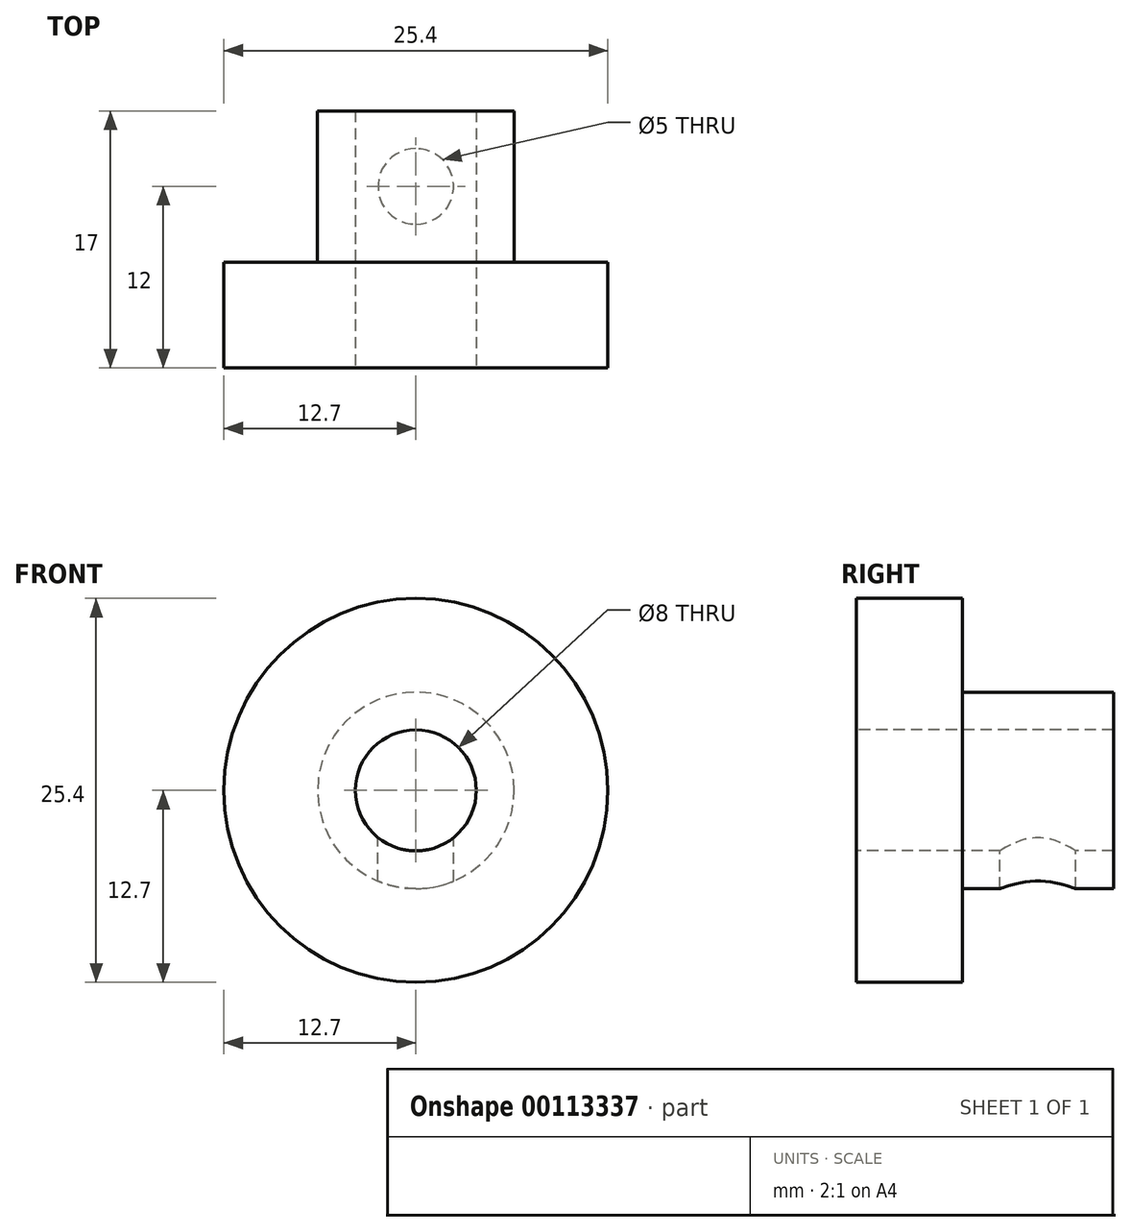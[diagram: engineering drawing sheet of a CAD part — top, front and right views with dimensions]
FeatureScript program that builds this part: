
annotation { "Feature Type Name" : "Feature", "Feature Type Description" : "" }
export const myFeature = defineFeature(function(context is Context, id is Id, definition is map)
    precondition{}
    {
        {
            var Q0;
            Q0=qCreatedBy(makeId("Front.planeOp"),FACE);
            var sketch = newSketch(context, id + "F0", { "sketchPlane" : qUnion([Q0])});
            skCircle(sketch, "E0", {"center": v(0, 0) * mm, "radius": 12.7 * mm});
            skSolve(sketch);
        }
        {
            var Q0;
            Q0=makeQuery(id+"F0.imprint","IMPRINT",FACE,{"disambiguationData":[TD([[makeQuery(id+"F0.imprint","IMPRINT",EDGE,{"derivedFrom":sQuery(id+"F0.wireOp",EDGE,"E0")}),1.0]])]});
            extrude(context, id + "F1", {"entities" : qUnion([Q0]), "depth" : 7 * mm});
        }
        {
            var Q0;
            Q0=qCreatedBy(makeId("Front.planeOp"),FACE);
            var sketch = newSketch(context, id + "F2", { "sketchPlane" : qUnion([Q0])});
            skCircle(sketch, "E1", {"center": v(0, 0) * mm, "radius": 6.5 * mm});
            skSolve(sketch);
        }
        {
            var Q0;
            Q0 = qSketchRegion(id + "F2", true);
            extrude(context, id + "F3", {"entities" : qUnion([Q0]), "operationType" : NewBodyOperationType.ADD, "oppositeDirection" : true, "depth" : 10 * mm});
        }
        {
            var Q0;
            Q0=qCreatedBy(makeId("Front.planeOp"),FACE);
            var sketch = newSketch(context, id + "F4", { "sketchPlane" : qUnion([Q0])});
            skCircle(sketch, "E2", {"center": v(0, 0) * mm, "radius": 4 * mm});
            skSolve(sketch);
        }
        {
            var Q0;
            Q0 = qSketchRegion(id + "F4", true);
            extrude(context, id + "F5", {"entities" : qUnion([Q0]), "operationType" : NewBodyOperationType.REMOVE, "endBound" : BoundingType.THROUGH_ALL, "oppositeDirection" : true, "depth" : 25 * mm});
        }
        {
            var Q0;
            Q0=makeQuery(id+"F5.boolean.opBoolean","COPY",FACE,{"derivedFrom":makeQuery(id+"F5.opExtrude","CAP_FACE",FACE,{"disambiguationData":[OSD([sQuery(id+"F4.wireOp",EDGE,"E2")])],"isStart":true})});
            extrude(context, id + "F6", {"entities" : qUnion([Q0]), "operationType" : NewBodyOperationType.REMOVE, "endBound" : BoundingType.THROUGH_ALL, "oppositeDirection" : true, "depth" : 25 * mm});
        }
        {
            var Q0;
            Q0=qCreatedBy(makeId("Top.planeOp"),FACE);
            var sketch = newSketch(context, id + "F7", { "sketchPlane" : qUnion([Q0])});
            skPoint(sketch, "E3", {"position": v(0, 5) * mm});
            skSolve(sketch);
        }
        {
            var Q0;
            Q0=sQuery(id+"F7.wireOp",VERTEX,"E3");
            var Q1;
            Q1=makeQuery(id+"F1.opExtrude","SWEPT_BODY",BODY,{"disambiguationData":[OSD([sQuery(id+"F0.wireOp",EDGE,"E0")])]});
            hole(context, id + "F8", {"style" : HoleStyle.SIMPLE, "endStyle" : HoleEndStyle.THROUGH, "holeDiameter" : 5 * mm, "locations" : qUnion([Q0]), "scope" : qUnion([Q1]), "isTappedThrough" : true});
        }
    });
